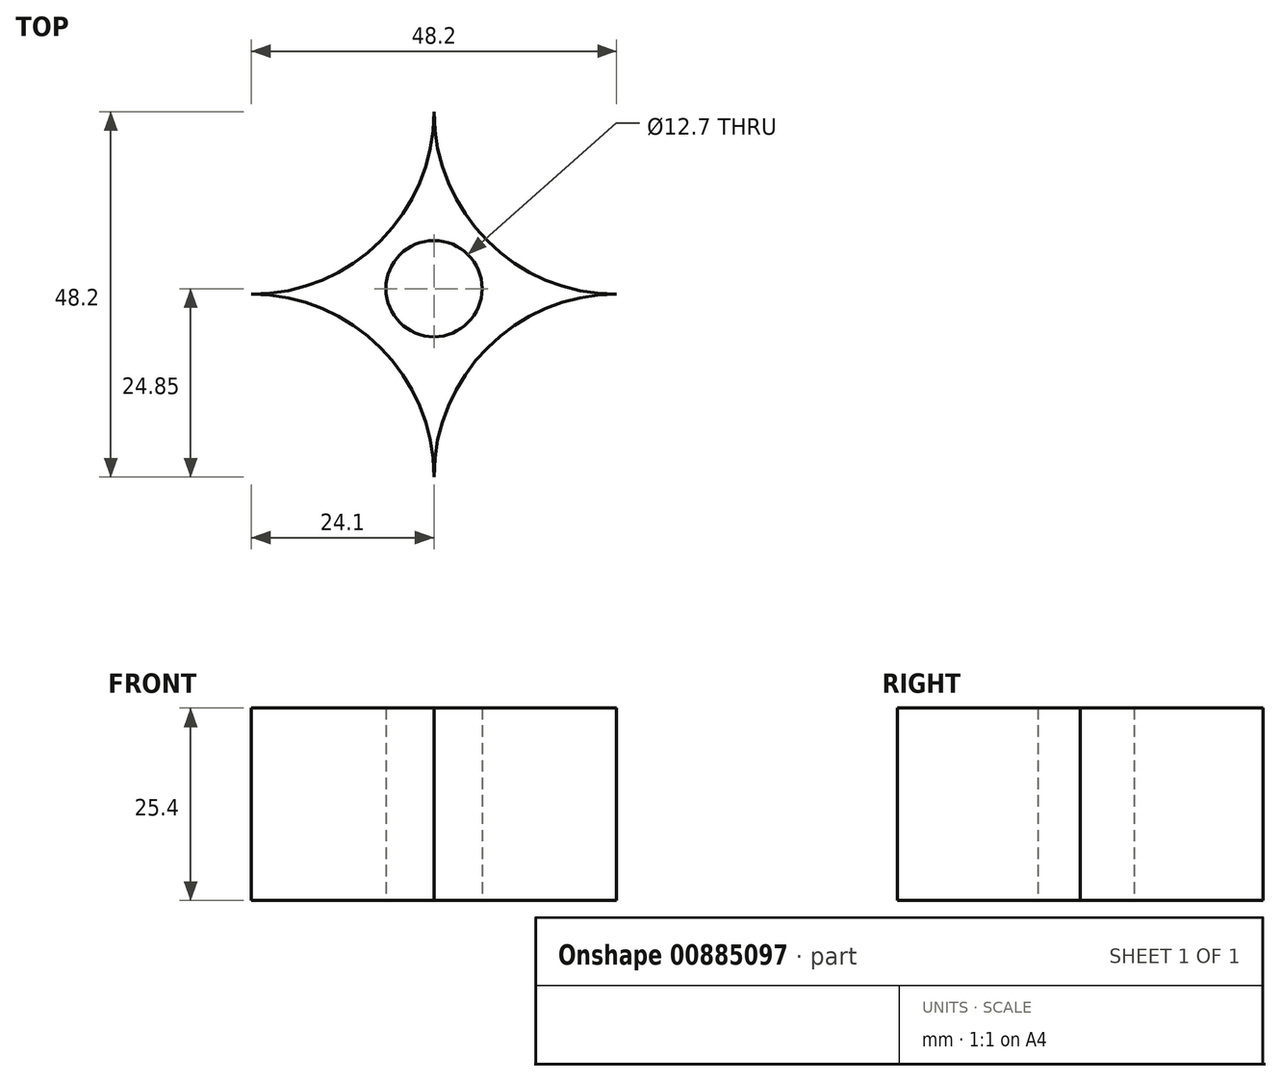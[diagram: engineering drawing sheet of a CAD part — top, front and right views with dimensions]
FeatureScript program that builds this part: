
annotation { "Feature Type Name" : "Feature", "Feature Type Description" : "" }
export const myFeature = defineFeature(function(context is Context, id is Id, definition is map)
    precondition{}
    {
        {
            var Q0;
            Q0=qCreatedBy(makeId("Top.planeOp"),FACE);
            var sketch = newSketch(context, id + "F0", { "sketchPlane" : qUnion([Q0])});
            skCircle(sketch, "E0", {"center": v(24.1, -24.85) * mm, "radius": 24.1 * mm});
            skCircle(sketch, "E1", {"center": v(24.1, 23.35) * mm, "radius": 24.1 * mm});
            skCircle(sketch, "E2.MirrorC", {"center": v(-24.1, 23.35) * mm, "radius": 24.1 * mm});
            skCircle(sketch, "E3.MirrorC", {"center": v(-24.1, -24.85) * mm, "radius": 24.1 * mm});
            skSolve(sketch);
        }
        {
            var Q0;
            {var subQ0=sQuery(id+"F0.wireOp",EDGE,"E3.MirrorC");var subQ1=sQuery(id+"F0.wireOp",EDGE,"E0");var subQ2=makeQuery(id+"F0.imprint","INTERSECT",VERTEX,{"derivedFrom":[subQ1,subQ0]});Q0=makeQuery(id+"F0.imprint","IMPRINT",FACE,{"disambiguationData":[TD([[makeQuery(id+"F0.imprint","IMPRINT",EDGE,{"disambiguationData":[TD([[subQ2,1.0]])],"derivedFrom":subQ1}),-1.0]])]});}
            extrude(context, id + "F1", {"entities" : qUnion([Q0]), "endBound" : BoundingType.SYMMETRIC, "depth" : 25.4 * mm, "offsetDistance" : 25.4 * mm});
        }
        {
            var Q0;
            Q0=makeQuery(id+"F1.opExtrude","CAP_FACE",FACE,{"disambiguationData":[OSD([sQuery(id+"F0.wireOp",EDGE,"E0"),sQuery(id+"F0.wireOp",EDGE,"E3.MirrorC"),sQuery(id+"F0.wireOp",EDGE,"E2.MirrorC"),sQuery(id+"F0.wireOp",EDGE,"E1")])],"isStart":false});
            var sketch = newSketch(context, id + "F2", { "sketchPlane" : qUnion([Q0])});
            skCircle(sketch, "E4", {"center": v(0, 10.68) * mm, "radius": 1.96 * mm});
            skCircle(sketch, "E5.1.0", {"center": v(-10.68, 0) * mm, "radius": 1.96 * mm});
            skCircle(sketch, "E5.2.0", {"center": v(0, -10.68) * mm, "radius": 1.96 * mm});
            skCircle(sketch, "E5.3.0", {"center": v(10.68, 0) * mm, "radius": 1.96 * mm});
            skPoint(sketch, "E5.center", {"position": v(0, 0) * mm});
            skSolve(sketch);
        }
        {
            var Q0;
            Q0=sQuery(id+"F2.wireOp",EDGE,"E5.2.0");
            var Q1;
            Q1=sQuery(id+"F2.wireOp",EDGE,"E5.1.0");
            var Q2;
            Q2=sQuery(id+"F2.wireOp",EDGE,"E4");
            var Q3;
            Q3=sQuery(id+"F2.wireOp",EDGE,"E5.3.0");
            extrude(context, id + "F3", {"bodyType" : ToolBodyType.SURFACE, "surfaceEntities" : qUnion([Q0, Q1, Q2, Q3]), "endBound" : BoundingType.SYMMETRIC, "oppositeDirection" : true, "depth" : 104.65 * mm, "offsetDistance" : 25.4 * mm});
        }
        {
            var Q0;
            Q0=makeQuery(id+"F1.opExtrude","CAP_FACE",FACE,{"disambiguationData":[OSD([sQuery(id+"F0.wireOp",EDGE,"E0"),sQuery(id+"F0.wireOp",EDGE,"E3.MirrorC"),sQuery(id+"F0.wireOp",EDGE,"E2.MirrorC"),sQuery(id+"F0.wireOp",EDGE,"E1")])],"isStart":true});
            var sketch = newSketch(context, id + "F4", { "sketchPlane" : qUnion([Q0])});
            skCircle(sketch, "E6", {"center": v(0, 0) * mm, "radius": 6.35 * mm});
            skSolve(sketch);
        }
        {
            var Q0;
            Q0=makeQuery(id+"F4.imprint","IMPRINT",FACE,{"disambiguationData":[TD([[makeQuery(id+"F4.imprint","IMPRINT",EDGE,{"derivedFrom":sQuery(id+"F4.wireOp",EDGE,"E6")}),1.0]])]});
            extrude(context, id + "F5", {"entities" : qUnion([Q0]), "operationType" : NewBodyOperationType.REMOVE, "endBound" : BoundingType.THROUGH_ALL, "oppositeDirection" : true, "depth" : 25.4 * mm, "offsetDistance" : 25.4 * mm});
        }
    });
